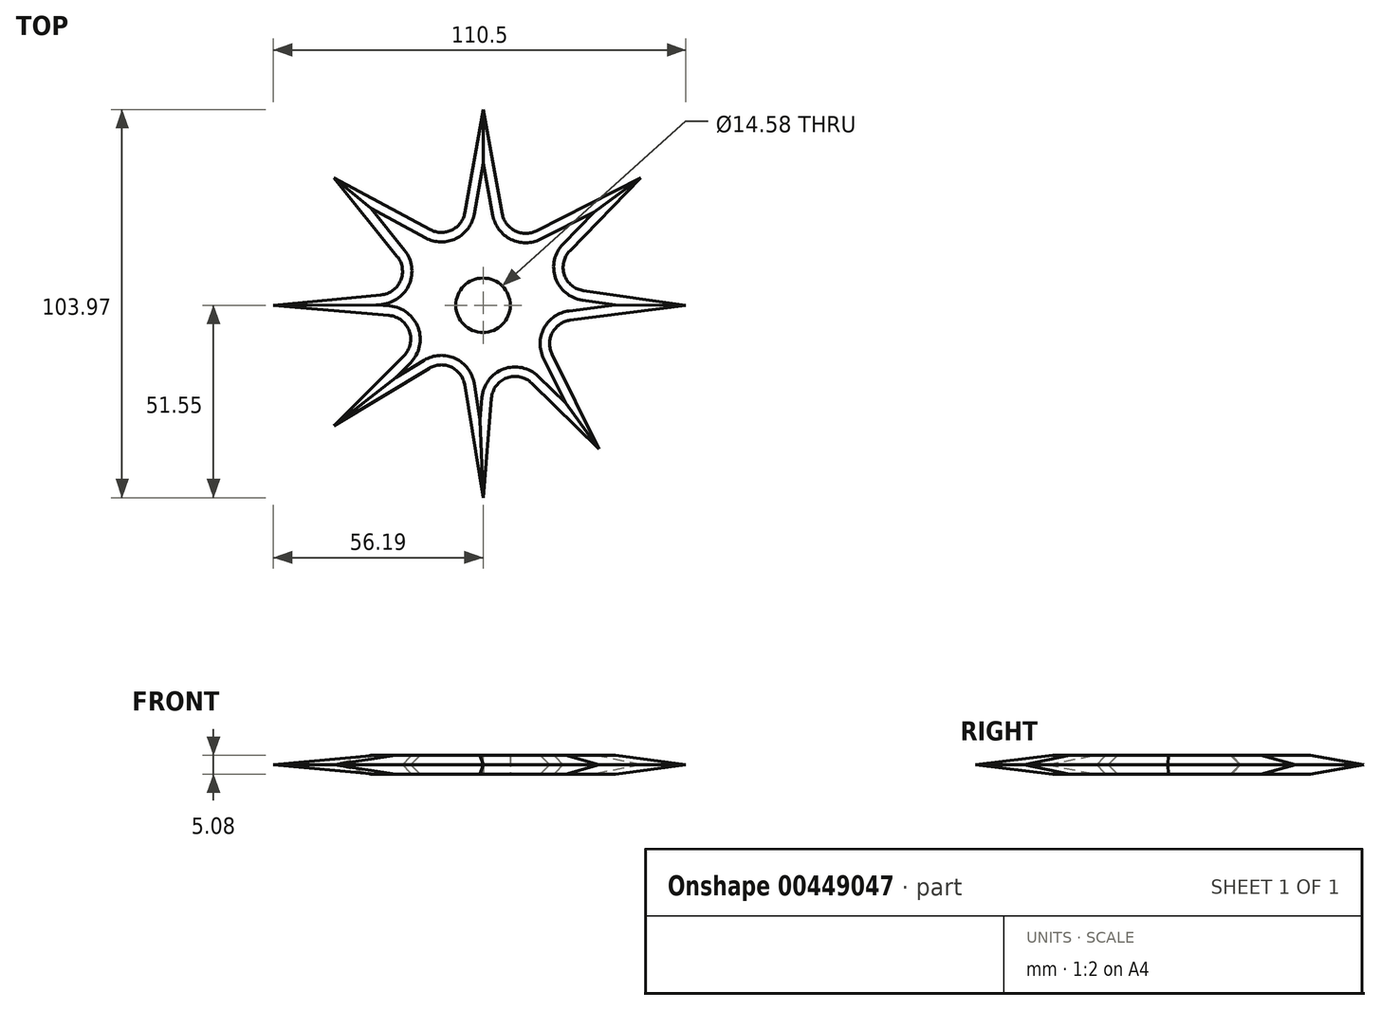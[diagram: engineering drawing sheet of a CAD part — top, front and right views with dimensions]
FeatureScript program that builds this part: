
annotation { "Feature Type Name" : "Feature", "Feature Type Description" : "" }
export const myFeature = defineFeature(function(context is Context, id is Id, definition is map)
    precondition{}
    {
        {
            var Q0;
            Q0=qCreatedBy(makeId("Top.planeOp"),FACE);
            var sketch = newSketch(context, id + "F0", { "sketchPlane" : qUnion([Q0])});
            skLineSegment(sketch, "E0", {"start": v(0, 0) * mm, "end": v(0, 52.42) * mm});
            skLineSegment(sketch, "E1", {"start": v(0, 0) * mm, "end": v(51.98, 0) * mm});
            skLineSegment(sketch, "E2", {"start": v(0, 0) * mm, "end": v(0, -51.55) * mm});
            skLineSegment(sketch, "E3", {"start": v(0, 0) * mm, "end": v(-56.19, 0) * mm});
            skLineSegment(sketch, "E4", {"start": v(0, 0) * mm, "end": v(-39.98, 34.12) * mm});
            skLineSegment(sketch, "E5", {"start": v(0, 0) * mm, "end": v(42.26, 34.12) * mm});
            skLineSegment(sketch, "E6", {"start": v(0, 0) * mm, "end": v(31.07, -38.48) * mm});
            skLineSegment(sketch, "E7", {"start": v(0, 0) * mm, "end": v(-39.98, -32.28) * mm});
            skLineSegment(sketch, "E8", {"start": v(42.26, 34.12) * mm, "end": v(14.26, 19.95) * mm});
            skLineSegment(sketch, "E9", {"start": v(42.26, 34.12) * mm, "end": v(23.25, 14.62) * mm});
            skLineSegment(sketch, "E10", {"start": v(26.9, 3.9) * mm, "end": v(54.3, 0) * mm});
            skLineSegment(sketch, "E11", {"start": v(54.3, 0) * mm, "end": v(23.35, -4.02) * mm});
            skLineSegment(sketch, "E12", {"start": v(18.48, -13.15) * mm, "end": v(31.07, -38.48) * mm});
            skLineSegment(sketch, "E13", {"start": v(31.07, -38.48) * mm, "end": v(13.01, -20.88) * mm});
            skLineSegment(sketch, "E14", {"start": v(2.26, -24.9) * mm, "end": v(0, -51.55) * mm});
            skLineSegment(sketch, "E15", {"start": v(0, -51.55) * mm, "end": v(-4.92, -21.3) * mm});
            skLineSegment(sketch, "E16", {"start": v(-14.46, -16.9) * mm, "end": v(-39.98, -32.28) * mm});
            skLineSegment(sketch, "E17", {"start": v(0, 52.42) * mm, "end": v(5.14, 24.47) * mm});
            skLineSegment(sketch, "E18", {"start": v(0, 52.42) * mm, "end": v(-4.9, 24.75) * mm});
            skLineSegment(sketch, "E19", {"start": v(-14.15, 20.27) * mm, "end": v(-39.98, 34.12) * mm});
            skLineSegment(sketch, "E20", {"start": v(-39.98, 34.12) * mm, "end": v(-23, 13.1) * mm});
            skLineSegment(sketch, "E21", {"start": v(-13.37, 0) * mm, "end": v(-56.19, 0) * mm});
            skLineSegment(sketch, "E22", {"start": v(-56.19, 0) * mm, "end": v(-27.32, 2.78) * mm});
            skLineSegment(sketch, "E23", {"start": v(-39.98, -32.28) * mm, "end": v(-21.23, -13.57) * mm});
            skLineSegment(sketch, "E24", {"start": v(-25.16, -2.75) * mm, "end": v(-56.19, 0) * mm});
            skCircle(sketch, "E25", {"center": v(0, 0) * mm, "radius": 7.3 * mm});
            skPoint(sketch, "E26.visualSharp", {"position": v(-6.42, 16.12) * mm});
            skArc(sketch, "E26.filletArc", {"start": v(-14.15, 20.27) * mm, "mid": v(-8.38, 20.15) * mm, "end": v(-4.9, 24.75) * mm});
            skPoint(sketch, "E27.visualSharp", {"position": v(6.68, 16.12) * mm});
            skArc(sketch, "E27.filletArc", {"start": v(5.14, 24.47) * mm, "mid": v(8.57, 19.93) * mm, "end": v(14.26, 19.95) * mm});
            skPoint(sketch, "E28.visualSharp", {"position": v(14.52, 5.66) * mm});
            skArc(sketch, "E28.filletArc", {"start": v(23.25, 14.62) * mm, "mid": v(21.79, 8.14) * mm, "end": v(26.9, 3.9) * mm});
            skPoint(sketch, "E29.visualSharp", {"position": v(14.52, -5.17) * mm});
            skArc(sketch, "E29.filletArc", {"start": v(23.35, -4.02) * mm, "mid": v(18.57, -7.33) * mm, "end": v(18.48, -13.15) * mm});
            skPoint(sketch, "E30.visualSharp", {"position": v(3.39, -11.5) * mm});
            skArc(sketch, "E30.filletArc", {"start": v(13.01, -20.88) * mm, "mid": v(6.36, -19.48) * mm, "end": v(2.26, -24.9) * mm});
            skPoint(sketch, "E31.visualSharp", {"position": v(-6.42, -12.04) * mm});
            skArc(sketch, "E31.filletArc", {"start": v(-4.92, -21.3) * mm, "mid": v(-8.52, -16.56) * mm, "end": v(-14.46, -16.9) * mm});
            skPoint(sketch, "E32.visualSharp", {"position": v(-11.6, -3.96) * mm});
            skArc(sketch, "E32.filletArc", {"start": v(-21.23, -13.57) * mm, "mid": v(-19.75, -6.91) * mm, "end": v(-25.16, -2.75) * mm});
            skPoint(sketch, "E33.visualSharp", {"position": v(-15.58, 3.91) * mm});
            skArc(sketch, "E33.filletArc", {"start": v(-27.32, 2.78) * mm, "mid": v(-22.08, 6.64) * mm, "end": v(-23, 13.1) * mm});
            skSolve(sketch);
        }
        {
            var Q0;
            Q0 = qSketchRegion(id + "F0", true);
            extrude(context, id + "F1", {"entities" : qUnion([Q0]), "depth" : 2.54 * mm});
        }
        {
            var Q0;
            Q0=makeQuery(id+"F1.opExtrude","CAP_EDGE",EDGE,{"disambiguationData":[OSD([sQuery(id+"F0.wireOp",EDGE,"E8")])],"isStart":false});
            var Q1;
            Q1=makeQuery(id+"F1.opExtrude","CAP_EDGE",EDGE,{"disambiguationData":[OSD([sQuery(id+"F0.wireOp",EDGE,"E10")])],"isStart":false});
            var Q2;
            Q2=makeQuery(id+"F1.opExtrude","CAP_EDGE",EDGE,{"disambiguationData":[OSD([sQuery(id+"F0.wireOp",EDGE,"E12")])],"isStart":false});
            var Q3;
            Q3=makeQuery(id+"F1.opExtrude","CAP_EDGE",EDGE,{"disambiguationData":[OSD([sQuery(id+"F0.wireOp",EDGE,"E13")])],"isStart":false});
            var Q4;
            Q4=makeQuery(id+"F1.opExtrude","CAP_EDGE",EDGE,{"disambiguationData":[OSD([sQuery(id+"F0.wireOp",EDGE,"E18")])],"isStart":false});
            var Q5;
            Q5=makeQuery(id+"F1.opExtrude","CAP_EDGE",EDGE,{"disambiguationData":[OSD([sQuery(id+"F0.wireOp",EDGE,"E20")])],"isStart":false});
            var Q6;
            Q6=makeQuery(id+"F1.opExtrude","CAP_EDGE",EDGE,{"disambiguationData":[OSD([sQuery(id+"F0.wireOp",EDGE,"E23")])],"isStart":false});
            var Q7;
            Q7=makeQuery(id+"F1.opExtrude","CAP_EDGE",EDGE,{"disambiguationData":[OSD([sQuery(id+"F0.wireOp",EDGE,"E15")])],"isStart":false});
            chamfer(context, id + "F2", {"entities" : qUnion([Q0, Q1, Q2, Q3, Q4, Q5, Q6, Q7]), "width" : 2.54 * mm, "tangentPropagation" : true});
        }
        {
            var Q0;
            Q0=makeQuery(id+"F1.opExtrude","SWEPT_BODY",BODY,{"disambiguationData":[OSD([sQuery(id+"F0.wireOp",EDGE,"E8"),sQuery(id+"F0.wireOp",EDGE,"E9"),sQuery(id+"F0.wireOp",EDGE,"E10"),sQuery(id+"F0.wireOp",EDGE,"E11"),sQuery(id+"F0.wireOp",EDGE,"E12"),sQuery(id+"F0.wireOp",EDGE,"E13"),sQuery(id+"F0.wireOp",EDGE,"E14"),sQuery(id+"F0.wireOp",EDGE,"E15"),sQuery(id+"F0.wireOp",EDGE,"E16"),sQuery(id+"F0.wireOp",EDGE,"E17"),sQuery(id+"F0.wireOp",EDGE,"E18"),sQuery(id+"F0.wireOp",EDGE,"E19"),sQuery(id+"F0.wireOp",EDGE,"E20"),sQuery(id+"F0.wireOp",EDGE,"E22"),sQuery(id+"F0.wireOp",EDGE,"E23"),sQuery(id+"F0.wireOp",EDGE,"E24"),sQuery(id+"F0.wireOp",EDGE,"E25"),sQuery(id+"F0.wireOp",EDGE,"E26.filletArc"),sQuery(id+"F0.wireOp",EDGE,"E27.filletArc"),sQuery(id+"F0.wireOp",EDGE,"E28.filletArc"),sQuery(id+"F0.wireOp",EDGE,"E29.filletArc"),sQuery(id+"F0.wireOp",EDGE,"E30.filletArc"),sQuery(id+"F0.wireOp",EDGE,"E31.filletArc"),sQuery(id+"F0.wireOp",EDGE,"E32.filletArc"),sQuery(id+"F0.wireOp",EDGE,"E33.filletArc")])]});
            var Q1;
            Q1=qCreatedBy(makeId("Top.planeOp"),FACE);
            mirror(context, id + "F3", {"operationType" : NewBodyOperationType.ADD, "entities" : qUnion([Q0]), "mirrorPlane" : qUnion([Q1])});
        }
    });
